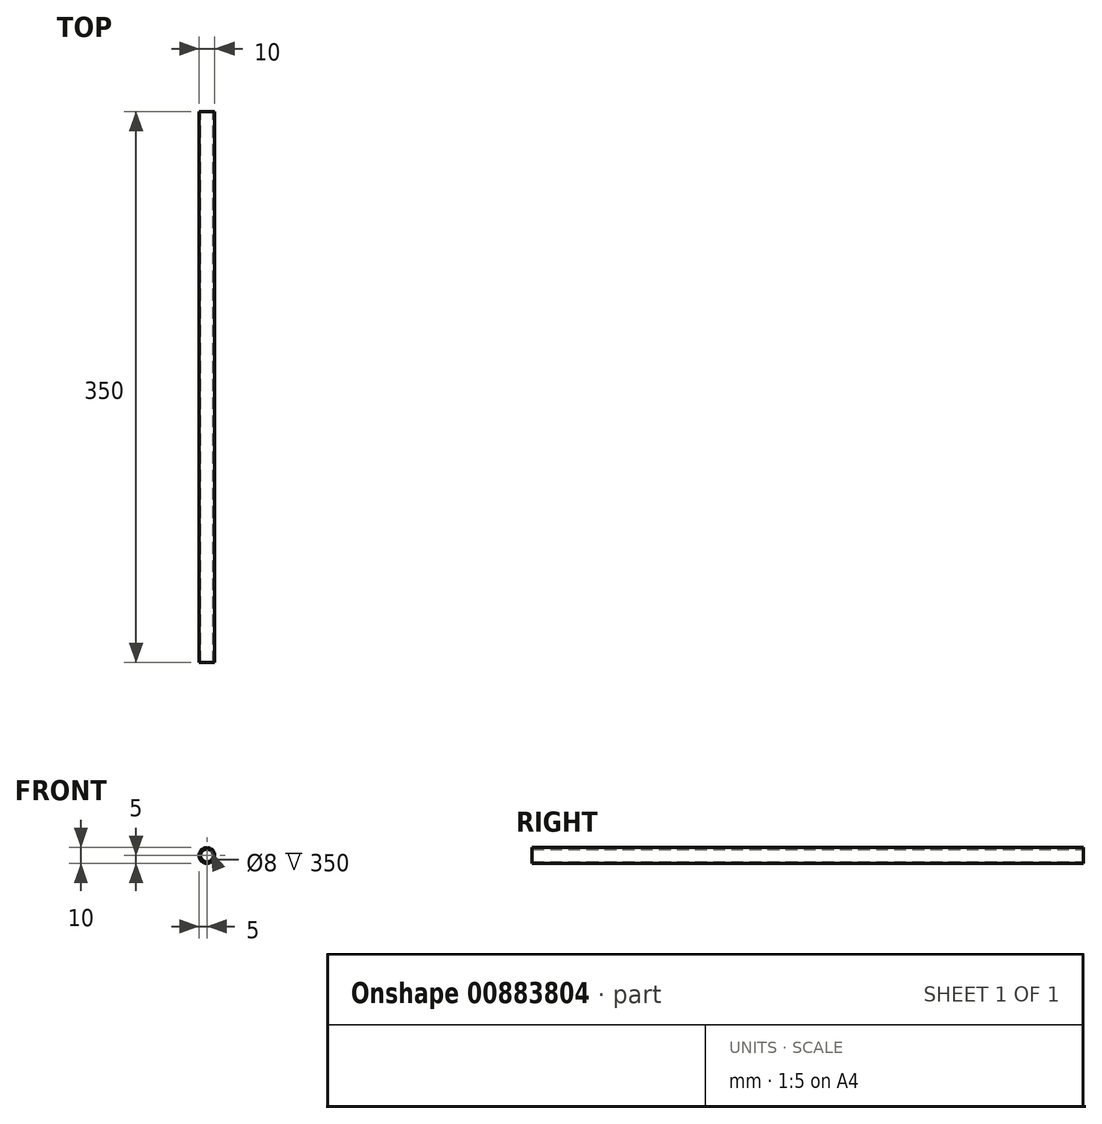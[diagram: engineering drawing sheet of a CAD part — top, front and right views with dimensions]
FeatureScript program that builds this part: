
annotation { "Feature Type Name" : "Feature", "Feature Type Description" : "" }
export const myFeature = defineFeature(function(context is Context, id is Id, definition is map)
    precondition{}
    {
        {
            var Q0;
            Q0=qCreatedBy(makeId("Front.planeOp"),FACE);
            var sketch = newSketch(context, id + "F0", { "sketchPlane" : qUnion([Q0])});
            skCircle(sketch, "E0", {"center": v(0, 0) * mm, "radius": 5 * mm});
            skCircle(sketch, "E1", {"center": v(0, 0) * mm, "radius": 4 * mm});
            skSolve(sketch);
        }
        {
            var Q0;
            Q0=makeQuery(id+"F0.imprint","IMPRINT",FACE,{"disambiguationData":[TD([[makeQuery(id+"F0.imprint","IMPRINT",EDGE,{"derivedFrom":sQuery(id+"F0.wireOp",EDGE,"E0")}),1.0]])]});
            extrude(context, id + "F1", {"entities" : qUnion([Q0]), "depth" : 350 * mm, "offsetDistance" : 25 * mm, "symmetric" : true});
        }
    });
